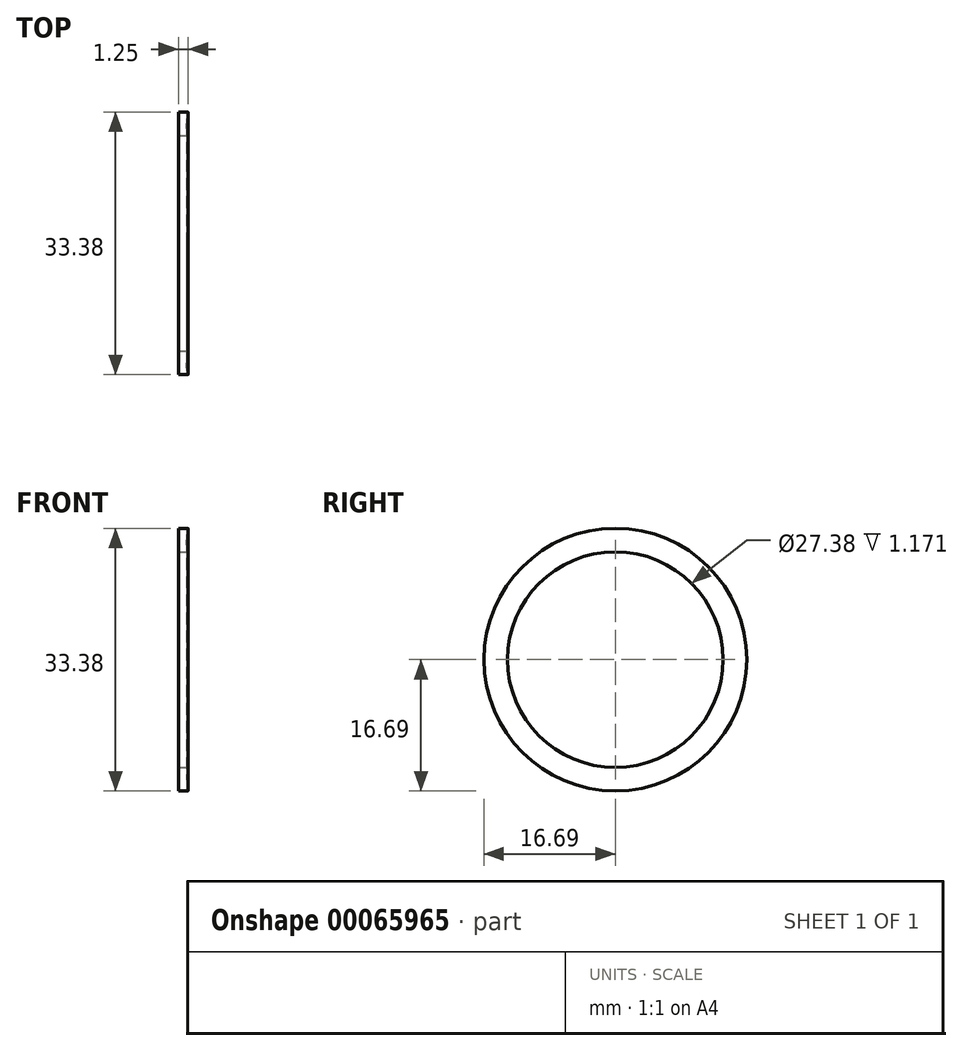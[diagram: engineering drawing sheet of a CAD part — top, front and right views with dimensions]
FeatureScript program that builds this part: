
annotation { "Feature Type Name" : "Feature", "Feature Type Description" : "" }
export const myFeature = defineFeature(function(context is Context, id is Id, definition is map)
    precondition{}
    {
        {
            var Q0;
            Q0=qCreatedBy(makeId("Front.planeOp"),FACE);
            var sketch = newSketch(context, id + "F0", { "sketchPlane" : qUnion([Q0])});
            skLineSegment(sketch, "E0.bottom", {"start": v(-0.1, 16.69) * mm, "end": v(-1.28, 16.69) * mm});
            skLineSegment(sketch, "E0.top", {"start": v(-0.1, 13.7) * mm, "end": v(-1.28, 13.7) * mm});
            skLineSegment(sketch, "E0.right", {"start": v(-1.28, 16.69) * mm, "end": v(-1.28, 13.7) * mm});
            skLineSegment(sketch, "E1", {"start": v(0, 0) * mm, "end": v(-6.16, 0) * mm, "construction": true});
            skArc(sketch, "E2", {"start": v(-0.03, 16.59) * mm, "mid": v(-0.26, 15.19) * mm, "end": v(-0.03, 13.8) * mm});
            skPoint(sketch, "E3.visualSharp", {"position": v(0, 16.69) * mm});
            skArc(sketch, "E3.filletArc", {"start": v(-0.03, 16.59) * mm, "mid": v(-0.05, 16.66) * mm, "end": v(-0.1, 16.69) * mm});
            skPoint(sketch, "E4.visualSharp", {"position": v(0, 13.7) * mm});
            skArc(sketch, "E4.filletArc", {"start": v(-0.1, 13.7) * mm, "mid": v(-0.05, 13.72) * mm, "end": v(-0.03, 13.8) * mm});
            skLineSegment(sketch, "E5", {"start": v(0, 13.7) * mm, "end": v(0, 0) * mm, "construction": true});
            skSolve(sketch);
        }
        {
            var Q0;
            Q0=makeQuery(id+"F0.imprint","IMPRINT",FACE,{"disambiguationData":[TD([[makeQuery(id+"F0.imprint","IMPRINT",EDGE,{"derivedFrom":sQuery(id+"F0.wireOp",EDGE,"E0.bottom")}),1.0]])]});
            var Q1;
            Q1=sQuery(id+"F0.wireOp",EDGE,"E1");
            revolve(context, id + "F1", {"entities" : qUnion([Q0]), "axis" : qUnion([Q1]), "revolveType" : RevolveType.FULL});
        }
    });
